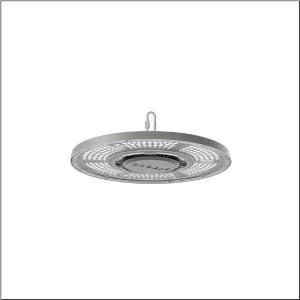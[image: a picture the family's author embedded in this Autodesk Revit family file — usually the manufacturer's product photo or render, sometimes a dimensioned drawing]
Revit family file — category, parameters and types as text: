
# Revit family: highbay_31-s_51hc417a4jmb
name_source: partatom
category: Lighting Fixtures
units: mm (PartAtom-declared; Revit-internal decimal feet)

## family parameters
Cut with Voids When Loaded = No
Host = Face
Light Source = No
Part Type = Normal
Room Calculation Point = No
Round Connector Dimension = Use Diameter
Shared = No

## types (1)
- Highbay 31-S (1 x LED, 20000 lm, 134 W, 4000K)
    Apparent Load = 134 VA
    CIE Flux Codes = 95 98 100 100 100
    Color Rendering = 80
    Color Temperature = 4000K
    Default Elevation = 1800 mm
    Description = Highbay 31-S, LED high bay luminaire, primary light control with lens, of PC, primary optical cover: cover panel, of PC, transparent, light emission: direct distribution, primary light characteristic: rotationally symmetric, installation type: suspended mounting, surface-mounted, LED, rated luminous flux: 20.000lm, luminous efficacy: 150lm/W, light colour: 840, colour temperature: 4000K, control gear: ECG, with cable, 3x 1.0mm², free wire ends, mains connection: 220..240V, AC/DC, 0/50..60Hz, cable length: 1,5m, rated input power: 134W, housing, rotationally symmetric, of diecast aluminium, powder-coated, grey aluminium (RAL 9007), with hook on luminaire side, incl. screw, diameter: 339mm, protection rating (complete): IP65, insulation class (complete): insulation class I (protective earthing), certification: CE, ENEC, UKCA, protection symbol: D, impact resistance: IK08, permissible operating ambient temperature: -30..+45°C, standard: EN 60598-2-22, EN 60598, corresponds to IFS (International Featured Standards) requirements for safety and quality in the food industry, packaging unit: 1 piece
    Height = 141 mm
    Lamp = 1 x LED
    Lamp Light Flux = 20000 lm
    Lamp Power = 134 W
    Lamp count = 1
    Length = 339 mm
    Luminous efficacy = 149 lm/W
    Manufacturer = Siteco
    ModVariant = No
    Model = 51HC417A4JMB
    Mounting Place = Ceiling
    Mounting Type = Pendant
    Number of Poles = 1
    OnlyDefault = Yes
    Power Factor = 1
    Product Name = Highbay 31-S
    Product group = LED high bay luminaire
    ProductGroupID = 903
    Protection Class = Protection class I
    Protection Degree = IP 65
    RLX_Detail_Level = 1
    RLX_Emergency_Light_Flux = 0 lm
    RLX_Emergency_Type = 0
    RLX_Emergency_Type_DB = No
    RlxData = <blob elided: 106193 chars, md5=345f9cdc>
    Socket = socket
    Standby Power = 0 W
    System Light Flux = 20000 lm
    System Power = 134 W
    Type Comments = Product without accessories
    Type Image = l_1007237.jpg
    URL = http://relux.com
    VarID = ---
    Voltage = 0 V
    Weight = 0.00 kg
    Width = 0 mm  [stored 0 ft]

note: [stored X ft] marks values corroborated as IEEE doubles in the binary element streams (Revit-internal decimal feet)

## geometry (parser evidence)
native form markers: Blend x4, Sweep x8
no freeform markers — native parametric forms only
